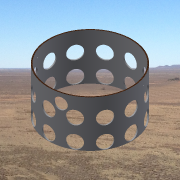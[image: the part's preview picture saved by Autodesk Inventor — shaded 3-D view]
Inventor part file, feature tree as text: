
AUTODESK INVENTOR PART (.ipt)
format: ipt  version: 2013 (Build 170138000, 138)  size: 386,560 bytes
history: native  units: in
note: dims shown in document units (in); Inventor stores cm internally (conversion verified against a paired STEP export)
features: sketch x9, plane x4, hole x3, extrude x2, pattern_circular x2, other x1
ambient origin geometry x8: Origin, YZ Plane, XZ Plane, XY Plane, X Axis, Y Axis, Z Axis, Center Point
bodies: Solid1 (feature_tree)
feature tree (21):
  extrude  "tube"  Depth=0.25in
  sketch  "Sketch2"  dims[d3=10.0in d4=0.0in d5=2.0in]
  other  "Work Point1"
  plane  "Work Plane1"
  hole  "spar"  [1 undecoded]
  pattern_circular  "spar pattern"  Count=12 Angle=360.0deg
  sketch  "Sketch7"  dims[d36=6.0in d45=0.0773in]
  plane  "Work Plane2"
  hole  "support"  [1 undecoded]
  pattern_circular  "support pattern"  Count=12 Angle=360.0deg
  sketch  "Sketch11"  dims[d63=1.5in]
  plane  "Work Plane3"
  extrude  "conduit"  Depth=8.0in
  sketch  "Sketch15"  dims[d74=2.4in d76=8.0in]
  plane  "Work Plane5"
  hole  "rebar"  [1 undecoded]
  sketch  "Sketch1"  dims[d0=18.0in d2=0.25in]
  sketch  "Sketch3"  dims[d17=2.875in d18=0.75in d19=0.375in d20=0.25in d21=0.5635in d22=1.0in d23=0.8108in d24=4.7244in d25=360.0deg]
  sketch  "Sketch10"  dims[d62=2.375in]
  sketch  "Sketch12"  dims[d64=2.875in d65=0.75in d66=0.375in d67=0.25in d68=0.5635in d69=1.0in d70=0.8108in d71=4.7244in d72=360.0deg]
  sketch  "Sketch16"  dims[d77=1.0in d78=0.0in d80=1.5in d81=0.25in d82=0.75in d83=0.375in d84=0.25in d85=0.5635in d86=1.0in d87=0.8108in]
note: 3 required parameter values undecoded (feature->parameter linkage not recoverable at this tier; creation-order binding heuristic only, values carry confidence <= 0.55)
